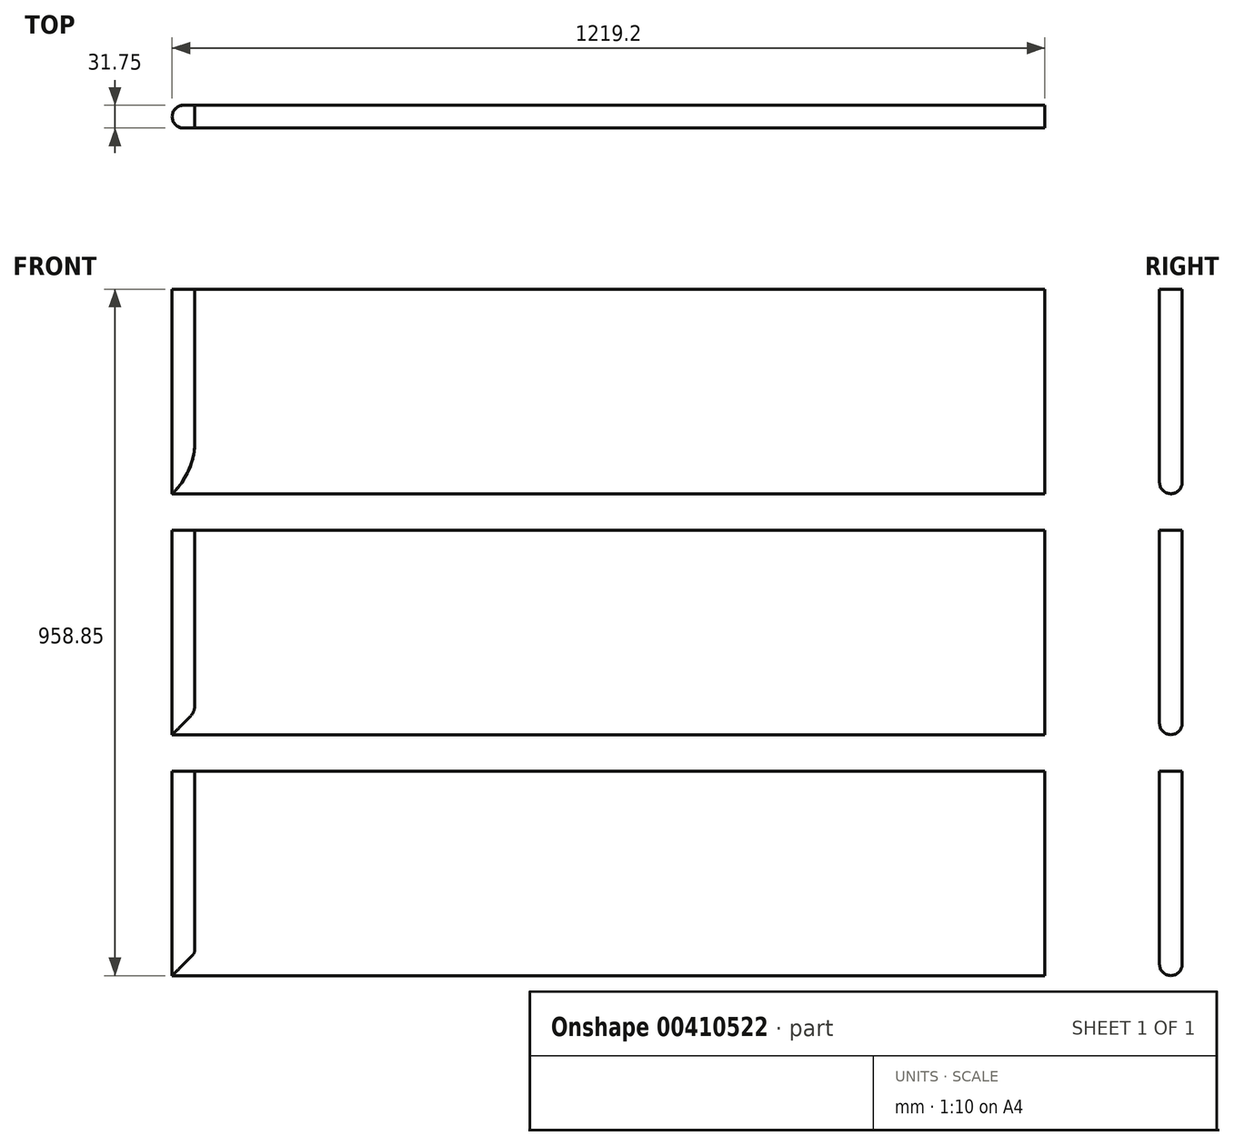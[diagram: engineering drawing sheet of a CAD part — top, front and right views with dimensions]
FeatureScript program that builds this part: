
annotation { "Feature Type Name" : "Feature", "Feature Type Description" : "" }
export const myFeature = defineFeature(function(context is Context, id is Id, definition is map)
    precondition{}
    {
        {
            var Q0;
            Q0=qCreatedBy(makeId("Front.planeOp"),FACE);
            var sketch = newSketch(context, id + "F0", { "sketchPlane" : qUnion([Q0])});
            skLineSegment(sketch, "E0.bottom", {"start": v(-595.6, 69.9) * mm, "end": v(623.6, 69.9) * mm});
            skLineSegment(sketch, "E0.top", {"start": v(-595.6, -215.85) * mm, "end": v(623.6, -215.85) * mm});
            skLineSegment(sketch, "E0.left", {"start": v(-595.6, 69.9) * mm, "end": v(-595.6, -215.85) * mm});
            skLineSegment(sketch, "E0.right", {"start": v(623.6, 69.9) * mm, "end": v(623.6, -215.85) * mm});
            skLineSegment(sketch, "E1", {"start": v(-563.84, 69.9) * mm, "end": v(-563.84, -142.07) * mm});
            skLineSegment(sketch, "E2.bottom", {"start": v(-595.6, -266.65) * mm, "end": v(623.6, -266.65) * mm});
            skLineSegment(sketch, "E2.top", {"start": v(-595.6, -552.4) * mm, "end": v(623.6, -552.4) * mm});
            skLineSegment(sketch, "E2.left", {"start": v(-595.6, -266.65) * mm, "end": v(-595.6, -552.4) * mm});
            skLineSegment(sketch, "E2.right", {"start": v(623.6, -266.65) * mm, "end": v(623.6, -552.4) * mm});
            skLineSegment(sketch, "E3", {"start": v(-563.84, -266.65) * mm, "end": v(-563.84, -510.13) * mm});
            skLineSegment(sketch, "E4.bottom", {"start": v(-595.6, -603.2) * mm, "end": v(623.6, -603.2) * mm});
            skLineSegment(sketch, "E4.top", {"start": v(-595.6, -888.95) * mm, "end": v(623.6, -888.95) * mm});
            skLineSegment(sketch, "E4.left", {"start": v(-595.6, -603.2) * mm, "end": v(-595.6, -888.95) * mm});
            skLineSegment(sketch, "E4.right", {"start": v(623.6, -603.2) * mm, "end": v(623.6, -888.95) * mm});
            skLineSegment(sketch, "E5", {"start": v(-563.84, -603.2) * mm, "end": v(-563.84, -851.94) * mm});
            skArc(sketch, "E6", {"start": v(-595.6, -215.85) * mm, "mid": v(-572.12, -182.24) * mm, "end": v(-563.84, -142.07) * mm});
            skLineSegment(sketch, "E7", {"start": v(-595.6, -552.4) * mm, "end": v(-571.28, -528.1) * mm});
            skArc(sketch, "E8.filletArc", {"start": v(-571.28, -528.1) * mm, "mid": v(-565.77, -519.85) * mm, "end": v(-563.84, -510.13) * mm});
            skLineSegment(sketch, "E9", {"start": v(-595.6, -888.95) * mm, "end": v(-567.56, -860.92) * mm});
            skArc(sketch, "E10.filletArc", {"start": v(-567.56, -860.92) * mm, "mid": v(-564.8, -856.8) * mm, "end": v(-563.84, -851.94) * mm});
            skSolve(sketch);
        }
        {
            var Q0;
            Q0=makeQuery(id+"F0.imprint","IMPRINT",FACE,{"disambiguationData":[TD([[makeQuery(id+"F0.imprint","IMPRINT",EDGE,{"derivedFrom":sQuery(id+"F0.wireOp",EDGE,"E0.top")}),1.0]])]});
            var Q1;
            Q1=makeQuery(id+"F0.imprint","IMPRINT",FACE,{"disambiguationData":[TD([[makeQuery(id+"F0.imprint","IMPRINT",EDGE,{"derivedFrom":sQuery(id+"F0.wireOp",EDGE,"E2.top")}),1.0]])]});
            var Q2;
            Q2=makeQuery(id+"F0.imprint","IMPRINT",FACE,{"disambiguationData":[TD([[makeQuery(id+"F0.imprint","IMPRINT",EDGE,{"derivedFrom":sQuery(id+"F0.wireOp",EDGE,"E4.top")}),1.0]])]});
            extrude(context, id + "F1", {"entities" : qUnion([Q0, Q1, Q2]), "depth" : 31.75 * mm});
        }
        {
            var Q0;
            {var subQ0=sQuery(id+"F0.wireOp",EDGE,"E0.left");Q0=makeQuery(id+"F0.imprint","IMPRINT",FACE,{"disambiguationData":[TD([[makeQuery(id+"F0.imprint","IMPRINT",EDGE,{"derivedFrom":subQ0}),1.0]])]});}
            var Q1;
            {var subQ0=sQuery(id+"F0.wireOp",EDGE,"E2.left");Q1=makeQuery(id+"F0.imprint","IMPRINT",FACE,{"disambiguationData":[TD([[makeQuery(id+"F0.imprint","IMPRINT",EDGE,{"derivedFrom":subQ0}),1.0]])]});}
            var Q2;
            {var subQ0=sQuery(id+"F0.wireOp",EDGE,"E4.left");Q2=makeQuery(id+"F0.imprint","IMPRINT",FACE,{"disambiguationData":[TD([[makeQuery(id+"F0.imprint","IMPRINT",EDGE,{"derivedFrom":subQ0}),1.0]])]});}
            extrude(context, id + "F2", {"entities" : qUnion([Q0, Q1, Q2]), "depth" : 31.75 * mm});
        }
        {
            var Q0;
            Q0=makeQuery(id+"F1.opExtrude","CAP_EDGE",EDGE,{"disambiguationData":[OSD([sQuery(id+"F0.wireOp",EDGE,"E4.top")])],"isStart":false});
            var Q1;
            Q1=makeQuery(id+"F2.opExtrude","CAP_EDGE",EDGE,{"disambiguationData":[OSD([sQuery(id+"F0.wireOp",EDGE,"E4.left")])],"isStart":false});
            var Q2;
            Q2=makeQuery(id+"F1.opExtrude","CAP_EDGE",EDGE,{"disambiguationData":[OSD([sQuery(id+"F0.wireOp",EDGE,"E4.top")])],"isStart":true});
            var Q3;
            Q3=makeQuery(id+"F2.opExtrude","CAP_EDGE",EDGE,{"disambiguationData":[OSD([sQuery(id+"F0.wireOp",EDGE,"E4.left")])],"isStart":true});
            var Q4;
            Q4=makeQuery(id+"F1.opExtrude","CAP_EDGE",EDGE,{"disambiguationData":[OSD([sQuery(id+"F0.wireOp",EDGE,"E2.top")])],"isStart":false});
            var Q5;
            Q5=makeQuery(id+"F1.opExtrude","CAP_EDGE",EDGE,{"disambiguationData":[OSD([sQuery(id+"F0.wireOp",EDGE,"E2.top")])],"isStart":true});
            var Q6;
            Q6=makeQuery(id+"F2.opExtrude","CAP_EDGE",EDGE,{"disambiguationData":[OSD([sQuery(id+"F0.wireOp",EDGE,"E2.left")])],"isStart":false});
            var Q7;
            Q7=makeQuery(id+"F2.opExtrude","CAP_EDGE",EDGE,{"disambiguationData":[OSD([sQuery(id+"F0.wireOp",EDGE,"E2.left")])],"isStart":true});
            var Q8;
            Q8=makeQuery(id+"F2.opExtrude","CAP_EDGE",EDGE,{"disambiguationData":[OSD([sQuery(id+"F0.wireOp",EDGE,"E0.left")])],"isStart":false});
            var Q9;
            Q9=makeQuery(id+"F1.opExtrude","CAP_EDGE",EDGE,{"disambiguationData":[OSD([sQuery(id+"F0.wireOp",EDGE,"E0.top")])],"isStart":false});
            var Q10;
            Q10=makeQuery(id+"F1.opExtrude","CAP_EDGE",EDGE,{"disambiguationData":[OSD([sQuery(id+"F0.wireOp",EDGE,"E0.top")])],"isStart":true});
            var Q11;
            Q11=makeQuery(id+"F2.opExtrude","CAP_EDGE",EDGE,{"disambiguationData":[OSD([sQuery(id+"F0.wireOp",EDGE,"E0.left")])],"isStart":true});
            fillet(context, id + "F3", {"entities" : qUnion([Q0, Q1, Q2, Q3, Q4, Q5, Q6, Q7, Q8, Q9, Q10, Q11]), "radius" : 15.88 * mm, "tangentPropagation" : true, "allowEdgeOverflow" : false});
        }
    });
